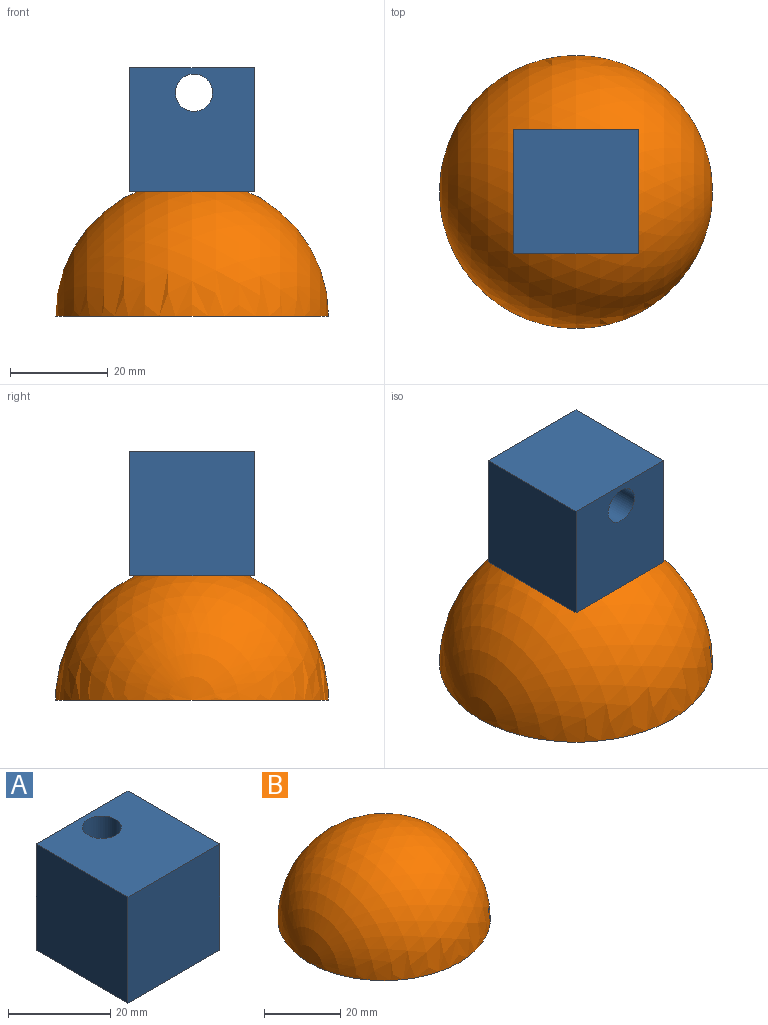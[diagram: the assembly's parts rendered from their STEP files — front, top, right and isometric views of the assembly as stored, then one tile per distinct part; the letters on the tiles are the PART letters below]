
ASSEMBLY  parts=2 mates=1
PART A: 7 faces, bbox 25.4x25.4x25.4 mm
  f0: plane 25.4x25.4mm, normal (0,0,-1), area 599.6mm2, adj f1,f3,f4,f5,f6
  f1: plane 25.4x25.4mm, normal (1,0,0), area 645.2mm2, adj f0,f2,f4,f5
  f2: plane 25.4x25.4mm, normal (0,0,1), area 599.6mm2, adj f1,f3,f4,f5,f6
  f3: plane 25.4x25.4mm, normal (-1,0,0), area 645.2mm2, adj f0,f2,f4,f5
  f4: plane 25.4x25.4mm, normal (0,-1,0), area 645.2mm2, adj f0,f1,f2,f3
  f5: plane 25.4x25.4mm, normal (0,1,0), area 645.2mm2, adj f0,f1,f2,f3
  f6: cylinder r=3.81mm len=25.4mm, axis (0,0,-1), area 608mm2, adj f0,f2
PART B: 3 faces, bbox 55.9x55.9x27.9 mm
  f0: sphere r=27.94mm, area 4904.9mm2, adj f1
  f1: plane 55.88x55.88mm, normal (0,0,-1), area 425.6mm2, adj f0,f2
  f2: sphere r=25.4mm, area 4053.7mm2, adj f1
PLACE A rot(axis=(1,0,0),90deg) t=(66.04,12.7,50.8)mm
PLACE B at identity
MATE fastened A.f4 <-> B.f0  axis (0,0,-1) through (27.94,0,25.4)mm
